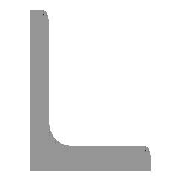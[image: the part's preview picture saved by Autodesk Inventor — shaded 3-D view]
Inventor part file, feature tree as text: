
AUTODESK INVENTOR PART (.ipt)
format: ipt  version: 2013 (Build 170138000, 138)  size: 129,024 bytes
history: native  units: mm (DEFAULTED — no unit token found)
features: other x4, plane x3, split x2, sketch x2
ambient origin geometry x8: Origin, YZ Plane, XZ Plane, XY Plane, X Axis, Y Axis, Z Axis, Center Point
bodies: Solid1 (feature_tree), Body (feature_tree)
feature tree (11):
  parser-record x1  (decoder bookkeeping rows leaked as tree rows — omitted from the tree; the rows remain in map.json)
  other  "Driven Length"
  other  "Start plane"
  other  "End plane"
  plane  "Work Plane4"
  split  "Split1"
  plane  "Work Plane5"
  split  "Split2"
  sketch  "Sketch3"  dims[d0=38.1mm]
  plane  "Work Plane3"
  sketch  "Sketch4"  dims[d1=38.1mm d2=4.7625mm d3=4.7625mm d4=1244.6mm d5=0.0mm d10=0.0mm d11=0.0mm d12=-0.0mm d13=1244.6mm d14=4.826mm d15=2.286mm d16=90.0deg d17=1244.6mm]
